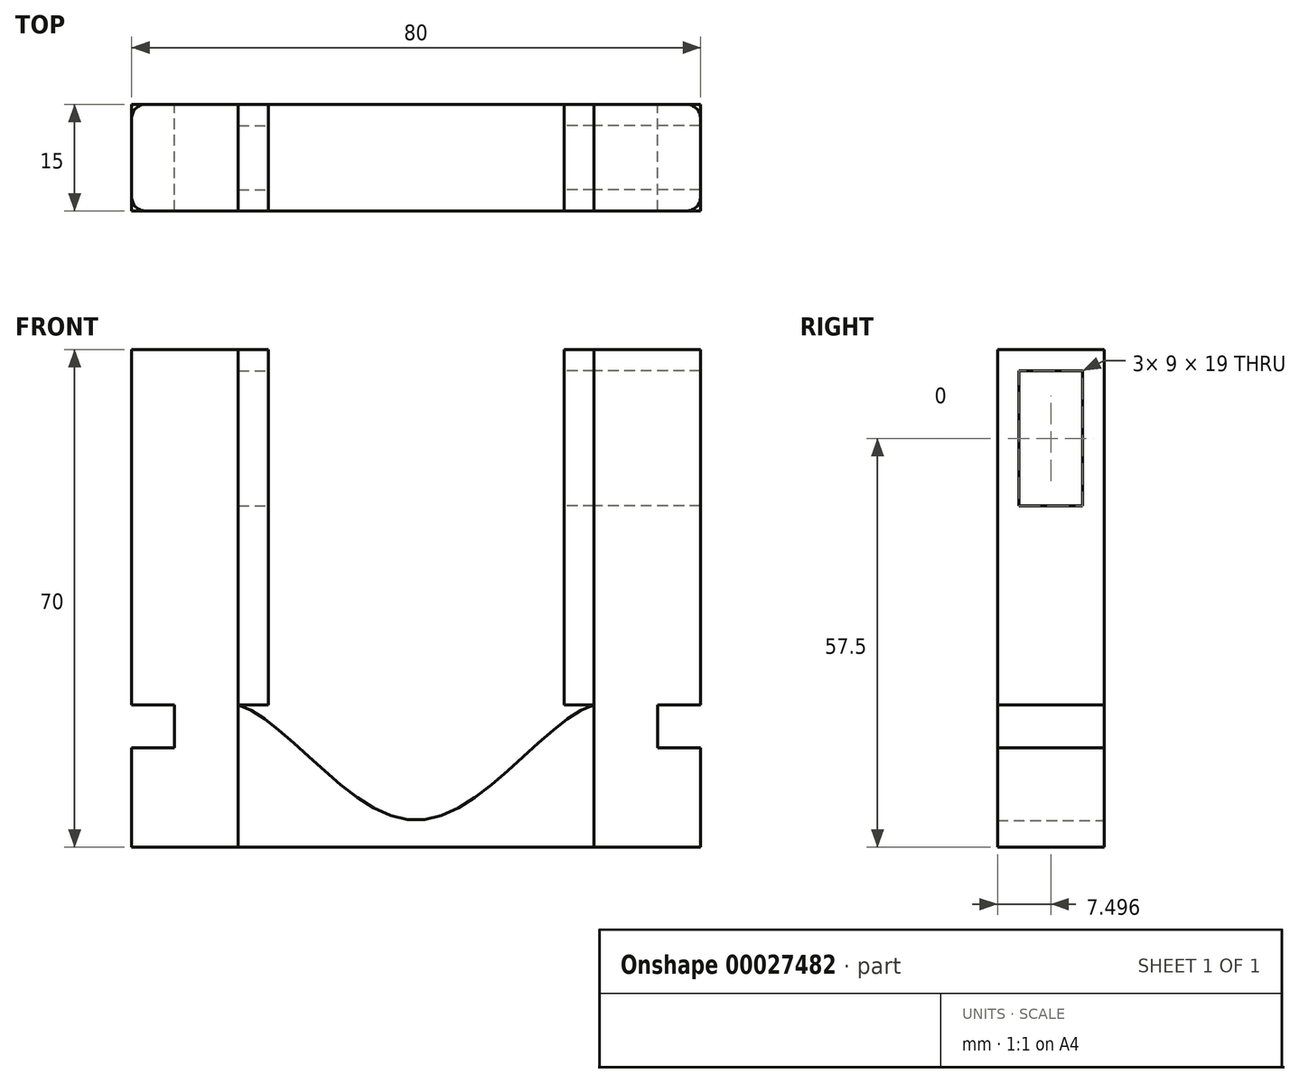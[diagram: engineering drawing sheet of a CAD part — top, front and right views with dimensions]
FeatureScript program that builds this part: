
annotation { "Feature Type Name" : "Feature", "Feature Type Description" : "" }
export const myFeature = defineFeature(function(context is Context, id is Id, definition is map)
    precondition{}
    {
        {
            var Q0;
            Q0=qCreatedBy(makeId("Top.planeOp"),FACE);
            var sketch = newSketch(context, id + "F0", { "sketchPlane" : qUnion([Q0])});
            skLineSegment(sketch, "E0.bottom", {"start": v(-25.06, 38.5) * mm, "end": v(-10.06, 38.5) * mm});
            skLineSegment(sketch, "E0.top", {"start": v(-25.06, 23.5) * mm, "end": v(-10.06, 23.5) * mm});
            skLineSegment(sketch, "E0.left", {"start": v(-25.06, 38.5) * mm, "end": v(-25.06, 23.5) * mm});
            skLineSegment(sketch, "E0.right", {"start": v(-10.06, 38.5) * mm, "end": v(-10.06, 23.5) * mm});
            skLineSegment(sketch, "E1.bottom", {"start": v(39.94, 38.5) * mm, "end": v(54.94, 38.5) * mm});
            skLineSegment(sketch, "E1.top", {"start": v(39.94, 23.5) * mm, "end": v(54.94, 23.5) * mm});
            skLineSegment(sketch, "E1.left", {"start": v(39.94, 38.5) * mm, "end": v(39.94, 23.5) * mm});
            skLineSegment(sketch, "E1.right", {"start": v(54.94, 38.5) * mm, "end": v(54.94, 23.5) * mm});
            skSolve(sketch);
        }
        {
            var Q0;
            Q0=makeQuery(id+"F0.imprint","IMPRINT",FACE,{"disambiguationData":[TD([[makeQuery(id+"F0.imprint","IMPRINT",EDGE,{"derivedFrom":sQuery(id+"F0.wireOp",EDGE,"E0.bottom")}),-1.0]])]});
            var Q1;
            Q1=makeQuery(id+"F0.imprint","IMPRINT",FACE,{"disambiguationData":[TD([[makeQuery(id+"F0.imprint","IMPRINT",EDGE,{"derivedFrom":sQuery(id+"F0.wireOp",EDGE,"E1.bottom")}),-1.0]])]});
            extrude(context, id + "F1", {"entities" : qUnion([Q0, Q1]), "depth" : 70 * mm});
        }
        {
            var Q0;
            Q0=makeQuery(id+"F1.opExtrude","SWEPT_FACE",FACE,{"disambiguationData":[OSD([sQuery(id+"F0.wireOp",EDGE,"E1.bottom")])]});
            var sketch = newSketch(context, id + "F2", { "sketchPlane" : qUnion([Q0])});
            skLineSegment(sketch, "E2.bottom", {"start": v(-39.94, 0) * mm, "end": v(10.06, 0) * mm});
            skLineSegment(sketch, "E2.left", {"start": v(-39.94, 0) * mm, "end": v(-39.94, 20) * mm});
            skLineSegment(sketch, "E2.right", {"start": v(10.06, 0) * mm, "end": v(10.06, 20) * mm});
            skFitSpline(sketch, "E3", {"points": [v(-39.94, 20) * mm, v(-14.94, 3.8) * mm, v(10.06, 20) * mm], "startDerivative": vector(40.2, -10.75) * mm, "endDerivative": vector(40.2, 10.75) * mm});
            skLineSegment(sketch, "E4", {"start": v(-14.94, 0) * mm, "end": v(-14.94, 60.06) * mm, "construction": true});
            skSolve(sketch);
        }
        {
            var Q0;
            Q0=makeQuery(id+"F2.imprint","IMPRINT",FACE,{"disambiguationData":[TD([[makeQuery(id+"F2.imprint","IMPRINT",EDGE,{"derivedFrom":sQuery(id+"F2.wireOp",EDGE,"E2.bottom")}),1.0]])]});
            extrude(context, id + "F3", {"entities" : qUnion([Q0]), "oppositeDirection" : true, "depth" : 15 * mm});
        }
        {
            var Q0;
            Q0=makeQuery(id+"F1.opExtrude","SWEPT_FACE",FACE,{"disambiguationData":[OSD([sQuery(id+"F0.wireOp",EDGE,"E1.bottom")])]});
            var sketch = newSketch(context, id + "F4", { "sketchPlane" : qUnion([Q0])});
            skLineSegment(sketch, "E5.bottom", {"start": v(-39.94, 70) * mm, "end": v(-34.24, 70) * mm});
            skLineSegment(sketch, "E5.top", {"start": v(-39.94, 55) * mm, "end": v(-34.24, 55) * mm});
            skLineSegment(sketch, "E5.left", {"start": v(-39.94, 70) * mm, "end": v(-39.94, 55) * mm});
            skLineSegment(sketch, "E5.right", {"start": v(-34.24, 70) * mm, "end": v(-34.24, 55) * mm});
            skLineSegment(sketch, "E6.bottom", {"start": v(10.06, 70) * mm, "end": v(4.36, 70) * mm});
            skLineSegment(sketch, "E6.top", {"start": v(10.06, 55) * mm, "end": v(4.36, 55) * mm});
            skLineSegment(sketch, "E6.left", {"start": v(10.06, 70) * mm, "end": v(10.06, 55) * mm});
            skLineSegment(sketch, "E6.right", {"start": v(4.36, 70) * mm, "end": v(4.36, 55) * mm});
            skSolve(sketch);
        }
        {
            var Q0;
            Q0=makeQuery(id+"F1.opExtrude","SWEPT_FACE",FACE,{"disambiguationData":[OSD([sQuery(id+"F0.wireOp",EDGE,"E0.bottom")])]});
            var sketch = newSketch(context, id + "F5", { "sketchPlane" : qUnion([Q0])});
            skLineSegment(sketch, "E7.bottom", {"start": v(25.06, 14) * mm, "end": v(19.06, 14) * mm});
            skLineSegment(sketch, "E7.top", {"start": v(25.06, 20) * mm, "end": v(19.06, 20) * mm});
            skLineSegment(sketch, "E7.right", {"start": v(19.06, 14) * mm, "end": v(19.06, 20) * mm});
            skSolve(sketch);
        }
        {
            var Q0;
            {var subQ2=sQuery(id+"F5.wireOp",EDGE,"E7.bottom");Q0=makeQuery(id+"F5.imprint","IMPRINT",FACE,{"disambiguationData":[TD([[makeQuery(id+"F5.imprint","IMPRINT",EDGE,{"derivedFrom":subQ2}),-1.0]])]});}
            extrude(context, id + "F6", {"entities" : qUnion([Q0]), "operationType" : NewBodyOperationType.REMOVE, "oppositeDirection" : true, "depth" : 25 * mm});
        }
        {
            var Q0;
            Q0=makeQuery(id+"F1.opExtrude","SWEPT_FACE",FACE,{"disambiguationData":[OSD([sQuery(id+"F0.wireOp",EDGE,"E1.bottom")])]});
            var sketch = newSketch(context, id + "F7", { "sketchPlane" : qUnion([Q0])});
            skLineSegment(sketch, "E8.bottom", {"start": v(-54.94, 14) * mm, "end": v(-48.94, 14) * mm});
            skLineSegment(sketch, "E8.top", {"start": v(-54.94, 20) * mm, "end": v(-48.94, 20) * mm});
            skLineSegment(sketch, "E8.right", {"start": v(-48.94, 14) * mm, "end": v(-48.94, 20) * mm});
            skSolve(sketch);
        }
        {
            var Q0;
            {var subQ2=sQuery(id+"F7.wireOp",EDGE,"E8.bottom");Q0=makeQuery(id+"F7.imprint","IMPRINT",FACE,{"disambiguationData":[TD([[makeQuery(id+"F7.imprint","IMPRINT",EDGE,{"derivedFrom":subQ2}),1.0]])]});}
            extrude(context, id + "F8", {"entities" : qUnion([Q0]), "operationType" : NewBodyOperationType.REMOVE, "oppositeDirection" : true, "depth" : 25 * mm});
        }
        {
            var Q0;
            Q0=makeQuery(id+"FCQL09DbcPnRoY9_3.opExtrude","SWEPT_EDGE",EDGE,{"disambiguationData":[OSD([sQuery(id+"F4.wireOp",EDGE,"E6.top"),sQuery(id+"F4.wireOp",EDGE,"E6.right")])]});
            var Q1;
            Q1=makeQuery(id+"FCQL09DbcPnRoY9_3.opExtrude","SWEPT_EDGE",EDGE,{"disambiguationData":[OSD([sQuery(id+"F4.wireOp",EDGE,"E6.bottom"),sQuery(id+"F4.wireOp",EDGE,"E6.right")])]});
            var Q2;
            Q2=makeQuery(id+"FCQL09DbcPnRoY9_3.opExtrude","SWEPT_EDGE",EDGE,{"disambiguationData":[OSD([sQuery(id+"F4.wireOp",EDGE,"E5.bottom"),sQuery(id+"F4.wireOp",EDGE,"E5.right")])]});
            var Q3;
            Q3=makeQuery(id+"FCQL09DbcPnRoY9_3.opExtrude","SWEPT_EDGE",EDGE,{"disambiguationData":[OSD([sQuery(id+"F4.wireOp",EDGE,"E5.top"),sQuery(id+"F4.wireOp",EDGE,"E5.right")])]});
            var Q4;
            {var subQ0=sQuery(id+"F0.wireOp",EDGE,"E0.bottom");var subQ1=sQuery(id+"F0.wireOp",EDGE,"E0.left");Q4=makeQuery(id+"F6.boolean.opBoolean","SPLIT",EDGE,{"disambiguationData":[TD([makeQuery(id+"F6.opExtrude","SWEPT_FACE",FACE,{"disambiguationData":[OSD([sQuery(id+"F5.wireOp",EDGE,"E7.top")])]})])],"derivedFrom":makeQuery(id+"F1.opExtrude","SWEPT_EDGE",EDGE,{"disambiguationData":[OSD([subQ0,subQ1])]})});}
            var Q5;
            {var subQ0=sQuery(id+"F0.wireOp",EDGE,"E0.top");var subQ1=sQuery(id+"F0.wireOp",EDGE,"E0.left");Q5=makeQuery(id+"F6.boolean.opBoolean","SPLIT",EDGE,{"disambiguationData":[TD([makeQuery(id+"F6.opExtrude","SWEPT_FACE",FACE,{"disambiguationData":[OSD([sQuery(id+"F5.wireOp",EDGE,"E7.top")])]})])],"derivedFrom":makeQuery(id+"F1.opExtrude","SWEPT_EDGE",EDGE,{"disambiguationData":[OSD([subQ0,subQ1])]})});}
            var Q6;
            {var subQ0=sQuery(id+"F0.wireOp",EDGE,"E1.bottom");var subQ1=sQuery(id+"F0.wireOp",EDGE,"E1.right");Q6=makeQuery(id+"F8.boolean.opBoolean","SPLIT",EDGE,{"disambiguationData":[TD([makeQuery(id+"F8.opExtrude","SWEPT_FACE",FACE,{"disambiguationData":[OSD([sQuery(id+"F7.wireOp",EDGE,"E8.top")])]})])],"derivedFrom":makeQuery(id+"F1.opExtrude","SWEPT_EDGE",EDGE,{"disambiguationData":[OSD([subQ0,subQ1])]})});}
            var Q7;
            {var subQ0=sQuery(id+"F0.wireOp",EDGE,"E1.top");var subQ1=sQuery(id+"F0.wireOp",EDGE,"E1.right");Q7=makeQuery(id+"F8.boolean.opBoolean","SPLIT",EDGE,{"disambiguationData":[TD([makeQuery(id+"F8.opExtrude","SWEPT_FACE",FACE,{"disambiguationData":[OSD([sQuery(id+"F7.wireOp",EDGE,"E8.top")])]})])],"derivedFrom":makeQuery(id+"F1.opExtrude","SWEPT_EDGE",EDGE,{"disambiguationData":[OSD([subQ0,subQ1])]})});}
            fillet(context, id + "F9", {"entities" : qUnion([Q0, Q1, Q2, Q3, Q4, Q5, Q6, Q7]), "radius" : 2 * mm, "tangentPropagation" : true, "allowEdgeOverflow" : false});
        }
        {
            var Q0;
            Q0=makeQuery(id+"F1.opExtrude","SWEPT_FACE",FACE,{"disambiguationData":[OSD([sQuery(id+"F0.wireOp",EDGE,"E0.bottom")])]});
            var sketch = newSketch(context, id + "F10", { "sketchPlane" : qUnion([Q0])});
            skLineSegment(sketch, "E9.bottom", {"start": v(10.06, 70) * mm, "end": v(5.86, 70) * mm});
            skLineSegment(sketch, "E9.top", {"start": v(10.06, 20) * mm, "end": v(5.86, 20) * mm});
            skLineSegment(sketch, "E9.left", {"start": v(10.06, 70) * mm, "end": v(10.06, 20) * mm});
            skLineSegment(sketch, "E9.right", {"start": v(5.86, 70) * mm, "end": v(5.86, 20) * mm});
            skPoint(sketch, "E10.0", {"position": v(10.06, 20) * mm});
            skPoint(sketch, "E11.0", {"position": v(-39.94, 70) * mm});
            skLineSegment(sketch, "E12.bottom", {"start": v(-39.94, 70) * mm, "end": v(-35.74, 70) * mm});
            skLineSegment(sketch, "E12.top", {"start": v(-39.94, 20) * mm, "end": v(-35.74, 20) * mm});
            skLineSegment(sketch, "E12.left", {"start": v(-39.94, 70) * mm, "end": v(-39.94, 20) * mm});
            skLineSegment(sketch, "E12.right", {"start": v(-35.74, 70) * mm, "end": v(-35.74, 20) * mm});
            skSolve(sketch);
        }
        {
            var Q0;
            Q0=makeQuery(id+"F10.imprint","IMPRINT",FACE,{"disambiguationData":[TD([[makeQuery(id+"F10.imprint","IMPRINT",EDGE,{"derivedFrom":sQuery(id+"F10.wireOp",EDGE,"E12.bottom")}),-1.0]])]});
            var Q1;
            Q1=makeQuery(id+"F10.imprint","IMPRINT",FACE,{"disambiguationData":[TD([[makeQuery(id+"F10.imprint","IMPRINT",EDGE,{"derivedFrom":sQuery(id+"F10.wireOp",EDGE,"E9.bottom")}),1.0]])]});
            var Q2;
            Q2=makeQuery(id+"F1.opExtrude","SWEPT_FACE",FACE,{"disambiguationData":[OSD([sQuery(id+"F0.wireOp",EDGE,"E0.top")])]});
            extrude(context, id + "F11", {"entities" : qUnion([Q0, Q1]), "endBound" : BoundingType.UP_TO_SURFACE, "oppositeDirection" : true, "endBoundEntityFace" : qUnion([Q2]), "depth" : 25 * mm});
        }
        {
            var Q0;
            Q0=makeQuery(id+"F11.opExtrude","SWEPT_FACE",FACE,{"disambiguationData":[OSD([sQuery(id+"F10.wireOp",EDGE,"E9.right")])]});
            var sketch = newSketch(context, id + "F12", { "sketchPlane" : qUnion([Q0])});
            skLineSegment(sketch, "E13.rect.bottom", {"start": v(35.5, 48) * mm, "end": v(26.5, 48) * mm});
            skLineSegment(sketch, "E13.rect.top", {"start": v(35.5, 67) * mm, "end": v(26.5, 67) * mm});
            skLineSegment(sketch, "E13.rect.left", {"start": v(35.5, 48) * mm, "end": v(35.5, 67) * mm});
            skLineSegment(sketch, "E13.rect.right", {"start": v(26.5, 48) * mm, "end": v(26.5, 67) * mm});
            skPoint(sketch, "E13.rect.middle", {"position": v(31, 57.5) * mm});
            skPoint(sketch, "E13.rect.middle.positionSnap0", {"position": v(31, 70) * mm});
            skPoint(sketch, "E13.rect.centerSnap0", {"position": v(31, 70) * mm});
            skSolve(sketch);
        }
        {
            var Q0;
            Q0=makeQuery(id+"F11.opExtrude","SWEPT_FACE",FACE,{"disambiguationData":[OSD([sQuery(id+"F10.wireOp",EDGE,"E12.right")])]});
            var sketch = newSketch(context, id + "F13", { "sketchPlane" : qUnion([Q0])});
            skLineSegment(sketch, "E14.rect.bottom", {"start": v(-26.5, 67) * mm, "end": v(-35.5, 67) * mm});
            skLineSegment(sketch, "E14.rect.top", {"start": v(-26.5, 48) * mm, "end": v(-35.5, 48) * mm});
            skLineSegment(sketch, "E14.rect.left", {"start": v(-26.5, 67) * mm, "end": v(-26.5, 48) * mm});
            skLineSegment(sketch, "E14.rect.right", {"start": v(-35.5, 67) * mm, "end": v(-35.5, 48) * mm});
            skPoint(sketch, "E14.rect.middle", {"position": v(-31, 57.5) * mm});
            skPoint(sketch, "E14.rect.middle.positionSnap0", {"position": v(-31, 70) * mm});
            skPoint(sketch, "E14.rect.centerSnap0", {"position": v(-31, 70) * mm});
            skPoint(sketch, "E15", {"position": v(-23.5, 45) * mm});
            skSolve(sketch);
        }
        {
            var Q0;
            Q0=makeQuery(id+"F13.imprint","IMPRINT",FACE,{"disambiguationData":[TD([[makeQuery(id+"F13.imprint","IMPRINT",EDGE,{"derivedFrom":sQuery(id+"F13.wireOp",EDGE,"E14.rect.bottom")}),1.0]])]});
            extrude(context, id + "F14", {"entities" : qUnion([Q0]), "operationType" : NewBodyOperationType.REMOVE, "oppositeDirection" : true, "depth" : 25 * mm});
        }
        {
            var Q0;
            Q0=makeQuery(id+"F12.imprint","IMPRINT",FACE,{"disambiguationData":[TD([[makeQuery(id+"F12.imprint","IMPRINT",EDGE,{"derivedFrom":sQuery(id+"F12.wireOp",EDGE,"E13.rect.bottom")}),-1.0]])]});
            extrude(context, id + "F15", {"entities" : qUnion([Q0]), "operationType" : NewBodyOperationType.REMOVE, "endBound" : BoundingType.UP_TO_NEXT, "oppositeDirection" : true, "depth" : 25 * mm});
        }
    });
